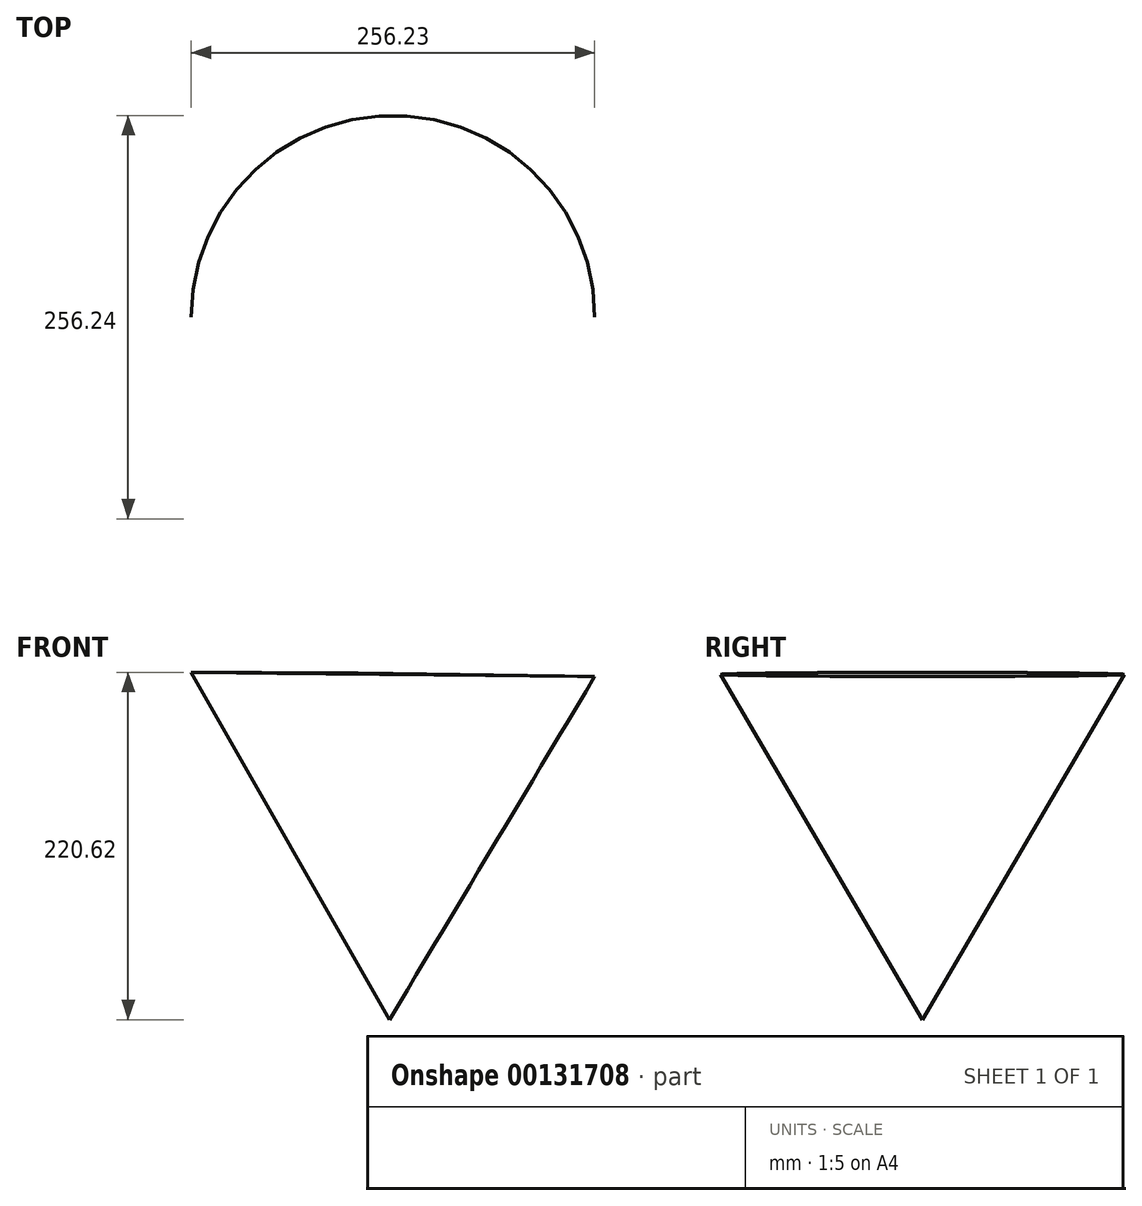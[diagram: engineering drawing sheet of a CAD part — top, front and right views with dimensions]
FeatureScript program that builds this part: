
annotation { "Feature Type Name" : "Feature", "Feature Type Description" : "" }
export const myFeature = defineFeature(function(context is Context, id is Id, definition is map)
    precondition{}
    {
        {
            var Q0;
            Q0=qCreatedBy(makeId("Front.planeOp"),FACE);
            var sketch = newSketch(context, id + "F0", { "sketchPlane" : qUnion([Q0])});
            skCircle(sketch, "E0.cCircle", {"center": v(0, 0) * mm, "radius": 73.32 * mm, "construction": true});
            skLineSegment(sketch, "E0.0", {"start": v(-2.25, -146.63) * mm, "end": v(-125.86, 75.26) * mm});
            skLineSegment(sketch, "E0.1", {"start": v(-125.86, 75.26) * mm, "end": v(128.11, 71.37) * mm});
            skLineSegment(sketch, "E0.2", {"start": v(128.11, 71.37) * mm, "end": v(-2.25, -146.63) * mm});
            skPoint(sketch, "E0.0.midPoint", {"position": v(-64.06, -35.68) * mm});
            skLineSegment(sketch, "E1", {"start": v(0, 73.33) * mm, "end": v(-2.25, -146.63) * mm});
            skSolve(sketch);
        }
        {
            var Q0;
            {var subQ0=sQuery(id+"F0.wireOp",EDGE,"E0.2");Q0=makeQuery(id+"F0.imprint","IMPRINT",FACE,{"disambiguationData":[TD([[makeQuery(id+"F0.imprint","IMPRINT",EDGE,{"derivedFrom":subQ0}),-1.0]])]});}
            var Q1;
            Q1=sQuery(id+"F0.wireOp",EDGE,"E1");
            revolve(context, id + "F1", {"entities" : qUnion([Q0]), "axis" : qUnion([Q1]), "revolveType" : RevolveType.FULL});
        }
    });
